# Revit family: PRD_FrankeWS_SpprtRls_FoldableGrabRail_CNTX70G,72F-R,72F-L
name_source: partatom
category: Specialty Equipment
revit_build: Autodesk Revit 2018 (Build: 20190510_1515(x64)
units: mm (PartAtom-declared; Revit-internal decimal feet)

## family parameters
Cut with Voids When Loaded = No
Host = Face
OmniClass Number = 23.40.20.21
OmniClass Title = Toilet and Bath Specialties
Part Type = Normal
Room Calculation Point = No
Round Connector Dimension = Use Diameter
Shared = No

## types (3) — shared parameters
ApparentLoad = 0 VA
AssetType = Fixed
Category = Pr_40_20_76_84, Support rails
Color = no colour
Default Elevation = 800 mm  [stored 2.62467 ft]
DurationUnit = year
EndingMaterial = PRD_AR_SyntheticBlack
Features = stainless steel, surface satin finished, rough polishing for better surface feel, prevention against unmeant folding, gum rubber stop absorber
Finish = satin finished
HiddenFixing = NO
Hinged = YES
IfcExportAs = IfcFurnitureType
IfcExportType = USERDEFINED
MainColor = stainless steel
Manufacturer = KWC Group AG
ManufacturerName = KWC Group AG
ManufacturerURL = www.kwc.com
Material = stainless steel
MaterialCode = 1.4301
MaterialFinish = Satin finished
MaterialsBody = Stainless steel 1.4301
NBSDescription = Support rails
NBSReference = 45-35-72/360
NominalDepth = 850 mm  [stored 2.78871 ft]
NominalHeight = 250 mm  [stored 0.82021 ft]
NominalWidth = 100 mm  [stored 0.328084 ft]
PipeDiameter = 32 mm  [stored 0.104987 ft]
ProductInformation = https://pim.kwc.com
RailMaterial = PRD_AR_StainlessSteel_SatinFinished
Size = 850 x 250 x 100 mm
TypeOfMounting = WALL-MOUNTING
URL = www.kwc.com
Uniclass2015Code = Pr_40_20_76_84
Uniclass2015Title = Support rails
Uniclass2015Version = Products v1.10
Version = 1
Voltage = 0 V
WarrantyDurationUnit = year
zero-valued in all types: Power factor

## per-type parameters (varying)
| type | BIMObjectName | Description | GrossWeight | ModelNumber | Name | NetWeight | Type |
| CNTX72F-R | PRD_AR_SpprtRls_FoldableGrabRail_CNTX72F-R | Foldable grab rail with electronic flush button for wall mounting, stainless steel, surface satin finished, material thickness 1.2 mm, flush button right, rough polishing for better surface feel, 32 mm pipe diameter, stirrup shape, integrated toilet roll holder, electronic flush button in front area, prevention against unmeant folding, gum rubber stop absorber, inspected and certified product, 4 mm thick mounting plate with three fixing holes, including stainless steel screws and dowels. Protection class: IP40. | 4.58 kg | 2000103283 | Foldable Grab Rail CNTX72F-R | 4.35 kg | CNTX72F |
| CNTX70G | PRD_AR_SpprtRls_FoldableGrabRail_CNTX70G | Foldable grab rail with flushing button for wall mounting, stainless steel, surface satin finished, rough polishing for better surface feel, 32 mm pipe diameter, material thickness 1.2 mm, integrated toilet roll holder, pneumatic flush button in front area, flush button optional on right or left side, prevention against unmeant folding, gum rubber stop absorber, inspected and certified product, 4 mm thick mounting plate with three fixing holes, included flushing mechanism contains 2 m pneumatic tube and set for assembling to Geberit cistern, incl. stainless steel screws and dowels. | 4.41 kg | 2030040945 | Foldable Grab Rail CNTX70G | 3.71 kg | CNTX70G |
| CNTX72F-L | PRD_AR_SpprtRls_FoldableGrabRail_CNTX72F-L | Foldable grab rail with electronic flush button for wall mounting, stainless steel, surface satin finished, material thickness 1.2 mm, flush button left, rough polishing for better surface feel, 32 mm pipe diameter, stirrup shape, integrated toilet roll holder, electronic flush button in front area, prevention against unmeant folding, gum rubber stop absorber, inspected and certified product, 4 mm thick mounting plate with three fixing holes, including stainless steel screws and dowels. Protection class: IP40. | 4.55 kg | 2000103284 | Foldable Grab Rail CNTX72F-L | 4.00 kg | CNTX72F |

note: column(s) folded — value = type name in every type: Model, ModelReference

note: [stored X ft] marks values corroborated as IEEE doubles in the binary element streams (Revit-internal decimal feet)

## geometry (parser evidence)
native form markers: Sweep x2
no freeform markers — native parametric forms only
